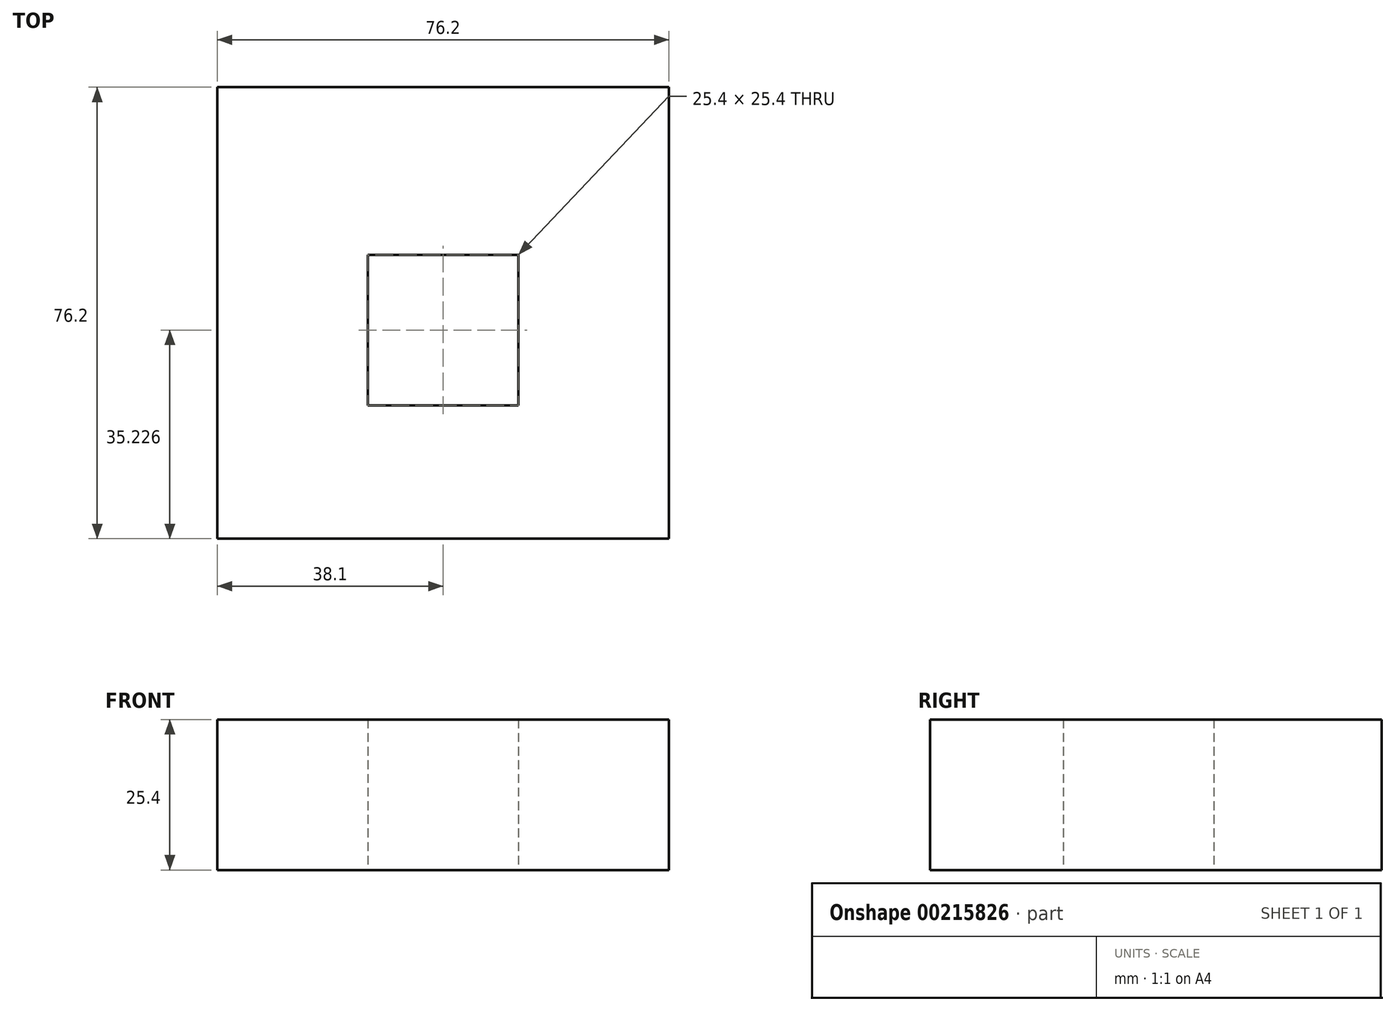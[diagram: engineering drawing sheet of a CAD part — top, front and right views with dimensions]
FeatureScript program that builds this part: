
annotation { "Feature Type Name" : "Feature", "Feature Type Description" : "" }
export const myFeature = defineFeature(function(context is Context, id is Id, definition is map)
    precondition{}
    {
        {
            var Q0;
            Q0=qCreatedBy(makeId("Top.planeOp"),FACE);
            var sketch = newSketch(context, id + "F0", { "sketchPlane" : qUnion([Q0])});
            skLineSegment(sketch, "E0.bottom", {"start": v(38.1, -38.1) * mm, "end": v(-38.1, -38.1) * mm});
            skLineSegment(sketch, "E0.top", {"start": v(38.1, 38.1) * mm, "end": v(-38.1, 38.1) * mm});
            skLineSegment(sketch, "E0.left", {"start": v(38.1, -38.1) * mm, "end": v(38.1, 38.1) * mm});
            skLineSegment(sketch, "E0.right", {"start": v(-38.1, -38.1) * mm, "end": v(-38.1, 38.1) * mm});
            skPoint(sketch, "E0.middle", {"position": v(0, 0) * mm});
            skLineSegment(sketch, "E1.bottom", {"start": v(12.7, -15.57) * mm, "end": v(-12.7, -15.57) * mm});
            skLineSegment(sketch, "E1.top", {"start": v(12.7, 9.83) * mm, "end": v(-12.7, 9.83) * mm});
            skLineSegment(sketch, "E1.left", {"start": v(12.7, -15.57) * mm, "end": v(12.7, 9.83) * mm});
            skLineSegment(sketch, "E1.right", {"start": v(-12.7, -15.57) * mm, "end": v(-12.7, 9.83) * mm});
            skPoint(sketch, "E1.middle", {"position": v(0, -2.87) * mm});
            skSolve(sketch);
        }
        {
            var Q0;
            Q0=makeQuery(id+"F0.imprint","IMPRINT",FACE,{"disambiguationData":[TD([[makeQuery(id+"F0.imprint","IMPRINT",EDGE,{"derivedFrom":sQuery(id+"F0.wireOp",EDGE,"E0.bottom")}),-1.0]])]});
            extrude(context, id + "F1", {"entities" : qUnion([Q0]), "depth" : 25.4 * mm});
        }
    });
